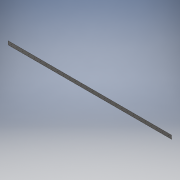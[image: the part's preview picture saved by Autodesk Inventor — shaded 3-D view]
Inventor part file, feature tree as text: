
AUTODESK INVENTOR PART (.ipt)
format: ipt  version: 2018 (Build 220112000, 112)  size: 215,040 bytes
history: native  units: mm
features: sketch x3, extrude x2, pattern_linear x1, hole x1
ambient origin geometry x8: Origin, YZ Plane, XZ Plane, XY Plane, X Axis, Y Axis, Z Axis, Center Point
bodies: Solid1 (feature_tree)
feature tree (7):
  extrude  "Extrusion1"  Depth=30.0mm
  extrude  "Extrusion2"  Depth=2.5mm
  pattern_linear  "Rectangular Pattern1"  Count1=140 Spacing1=0.0mm
  hole  "Hole1"  [1 undecoded]
  sketch  "Sketch1"  dims[d0=1.0mm d1=30.0mm]
  sketch  "Sketch2"  dims[d2=2.5mm d3=2.5mm]
  sketch  "Sketch3"  dims[d4=3.5mm d5=1400.0mm d6=0.0mm d7=25.0mm d8=3.25mm d9=1400.0mm d10=0.0mm d11=280.0mm d13=50.0mm d14=25.0mm d15=280.0mm d17=50.0mm d18=10.0mm d20=10.0mm d22=3.0mm d23=6.0mm d24=5.0mm d25=2.0mm d26=90.0deg d27=8.0mm d28=20.594885mm]
note: 1 required parameter value undecoded (feature->parameter linkage not recoverable at this tier; creation-order binding heuristic only, values carry confidence <= 0.55)
